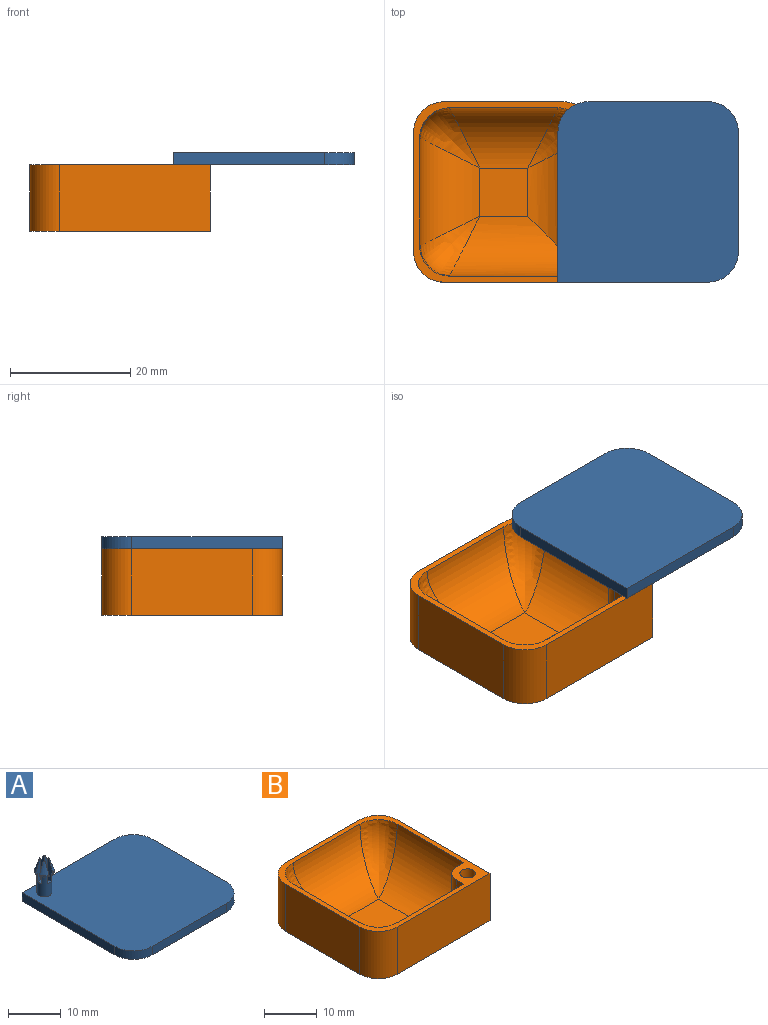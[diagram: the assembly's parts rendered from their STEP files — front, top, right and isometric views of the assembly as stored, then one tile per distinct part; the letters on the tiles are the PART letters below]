
ASSEMBLY  parts=2 mates=1
PART A: 35 faces, bbox 30.2x30.2x10.2 mm
  f0: cylinder r=1.4mm len=5mm, axis (0,0,-1), area 35.9mm2, adj f8,f9,f10,f15,f21,f22,f23,f24
  f1: cylinder r=1.9mm len=1.35mm, axis (0,0,-1), area 0.5mm2, adj f8,f23,f24,f33
  f2: cylinder r=1.9mm len=1.35mm, axis (0,0,-1), area 0.5mm2, adj f9,f27,f28,f31
  f3: cylinder r=1.9mm len=1.35mm, axis (0,0,-1), area 0.5mm2, adj f21,f25,f26,f32
  f4: cylinder r=1.9mm len=1.35mm, axis (0,0,-1), area 0.5mm2, adj f10,f29,f30,f34
  f5: plane 0.26x0.26mm, normal (0,0,1), area 0mm2, adj f23,f24,f33
  f6: plane 0.26x0.26mm, normal (0,0,1), area 0mm2, adj f27,f28,f31
  f7: plane 0.26x0.26mm, normal (0,0,1), area 0mm2, adj f29,f30,f34
  f8: plane 1.35x1.34mm, normal (0,0,-1), area 0.8mm2, adj f0,f1,f23,f24
  f9: plane 1.35x1.34mm, normal (0,0,-1), area 0.8mm2, adj f0,f2,f27,f28
  f10: plane 1.35x1.34mm, normal (0,0,-1), area 0.8mm2, adj f0,f4,f29,f30
  f11: plane 25x2mm, normal (-1,0,0), area 50mm2, adj f14,f15,f16,f17
  f12: plane 20x2mm, normal (0,-1,0), area 40mm2, adj f15,f16,f17,f18
  f13: plane 20x2mm, normal (1,0,0), area 40mm2, adj f15,f16,f18,f19
  f14: plane 25x2mm, normal (0,1,0), area 50mm2, adj f11,f15,f16,f19
  f15: plane 30x30mm, normal (0,0,1), area 877.7mm2, adj f0,f11,f12,f13,f14,f17,f18,f19
  f16: plane 30x30mm, normal (0,0,-1), area 883.9mm2, adj f11,f12,f13,f14,f17,f18,f19
  f17: cylinder r=5mm len=5mm, axis (0,0,-1), area 15.7mm2, adj f11,f12,f15,f16
  f18: cylinder r=5mm len=5mm, axis (0,0,1), area 15.7mm2, adj f12,f13,f15,f16
  f19: cylinder r=5mm len=5mm, axis (0,0,-1), area 15.7mm2, adj f13,f14,f15,f16
  f20: plane 0.26x0.26mm, normal (0,0,1), area 0mm2, adj f25,f26,f32
  f21: plane 1.35x1.34mm, normal (0,0,-1), area 0.8mm2, adj f0,f3,f25,f26
  f22: plane 2.8x2.8mm, normal (0,0,1), area 4.4mm2, adj f0,f23,f24,f25,f26,f27,f28,f29
  f23: plane 5.17x1.5mm, normal (0,-1,0), area 4.2mm2, adj f0,f1,f5,f8,f22,f24,f33
  f24: plane 5.17x1.52mm, normal (-1,0,0), area 4.2mm2, adj f0,f1,f5,f8,f22,f23,f33
  f25: plane 5.17x1.52mm, normal (1,0,0), area 4.2mm2, adj f0,f3,f20,f21,f22,f26,f32
  f26: plane 5.17x1.5mm, normal (0,-1,0), area 4.2mm2, adj f0,f3,f20,f21,f22,f25,f32
  f27: plane 5.17x1.5mm, normal (0,1,0), area 4.2mm2, adj f0,f2,f6,f9,f22,f28,f31
  f28: plane 5.17x1.52mm, normal (1,0,0), area 4.2mm2, adj f0,f2,f6,f9,f22,f27,f31
  f29: plane 5.17x1.52mm, normal (-1,0,0), area 4.2mm2, adj f0,f4,f7,f10,f22,f30,f34
  f30: plane 5.17x1.5mm, normal (0,1,0), area 4.2mm2, adj f0,f4,f7,f10,f22,f29,f34
  f31: cone r=0.9mm half-angle=20deg, axis (0,0,-1), area 3.1mm2, adj f2,f6,f27,f28
  f32: cone r=0.9mm half-angle=20deg, axis (0,0,-1), area 3.1mm2, adj f3,f20,f25,f26
  f33: cone r=0.9mm half-angle=20deg, axis (0,0,-1), area 3.1mm2, adj f1,f5,f23,f24
  f34: cone r=0.9mm half-angle=20deg, axis (0,0,-1), area 3.1mm2, adj f4,f7,f29,f30
PART B: 24 faces, bbox 30x30x12.9 mm
  f0: cylinder r=10mm len=18.88mm, axis (1,0,0), area 242.6mm2, adj f5,f7,f14,f16,f17,f23
  f1: plane 20x11mm, normal (-1,0,0), area 220mm2, adj f5,f6,f8,f10
  f2: plane 25x11mm, normal (0,-1,0), area 275mm2, adj f3,f5,f6,f8
  f3: plane 25x11mm, normal (1,0,0), area 275mm2, adj f2,f5,f6,f9
  f4: plane 20x11mm, normal (0,1,0), area 220mm2, adj f5,f6,f9,f10
  f5: plane 30x30mm, normal (0,0,1), area 132mm2, adj f0,f1,f2,f3,f4,f8,f9,f10
  f6: plane 30x30mm, normal (0,0,-1), area 883.9mm2, adj f1,f2,f3,f4,f8,f9,f10
  f7: plane 8x8mm, normal (0,0,1), area 64mm2, adj f0,f12,f13,f16
  f8: cylinder r=5mm len=11mm, axis (0,0,-1), area 86.4mm2, adj f1,f2,f5,f6
  f9: cylinder r=5mm len=11mm, axis (0,0,-1), area 86.4mm2, adj f3,f4,f5,f6
  f10: cylinder r=5mm len=11mm, axis (0,0,1), area 86.4mm2, adj f1,f4,f5,f6
  f11: bspline ~11.94x10mm, area 82.5mm2, adj f5,f12,f13
  f12: cylinder r=10mm len=18mm, axis (0,-1,0), area 225.7mm2, adj f5,f7,f11,f14
  f13: cylinder r=10mm len=18mm, axis (-1,0,0), area 225.7mm2, adj f5,f7,f11,f15
  f14: bspline ~11.94x10mm, area 82.5mm2, adj f0,f5,f12
  f15: bspline ~11.94x10mm, area 82.5mm2, adj f5,f13,f16
  f16: cylinder r=10mm len=18.88mm, axis (0,1,0), area 242.6mm2, adj f0,f5,f7,f15,f18,f23
  f17: plane 6x2mm, normal (-1,0,0), area 8.2mm2, adj f0,f5,f23
  f18: plane 6x2mm, normal (0,1,0), area 8.2mm2, adj f5,f16,f23
  f19: cylinder r=1.5mm len=5mm, axis (0,0,1), area 47.1mm2, adj f5,f22
  f20: cylinder r=2mm len=4mm, axis (0,0,1), area 50.3mm2, adj f21,f22
  f21: plane 4x4mm, normal (0,0,1), area 12.6mm2, adj f20
  f22: plane 4x4mm, normal (0,0,-1), area 5.5mm2, adj f19,f20
  f23: cylinder r=3mm len=8.09mm, axis (0,0,-1), area 33.9mm2, adj f0,f5,f16,f17,f18
PLACE A rot(axis=(1,0,0),180deg) t=(23.23,-5.54,5.36)mm
PLACE B t=(-0.77,-5.54,-7.64)mm
MATE revolute A.f0 <-> B.f19  axis (0,0,1) through (11.23,-17.54,3.36)mm
